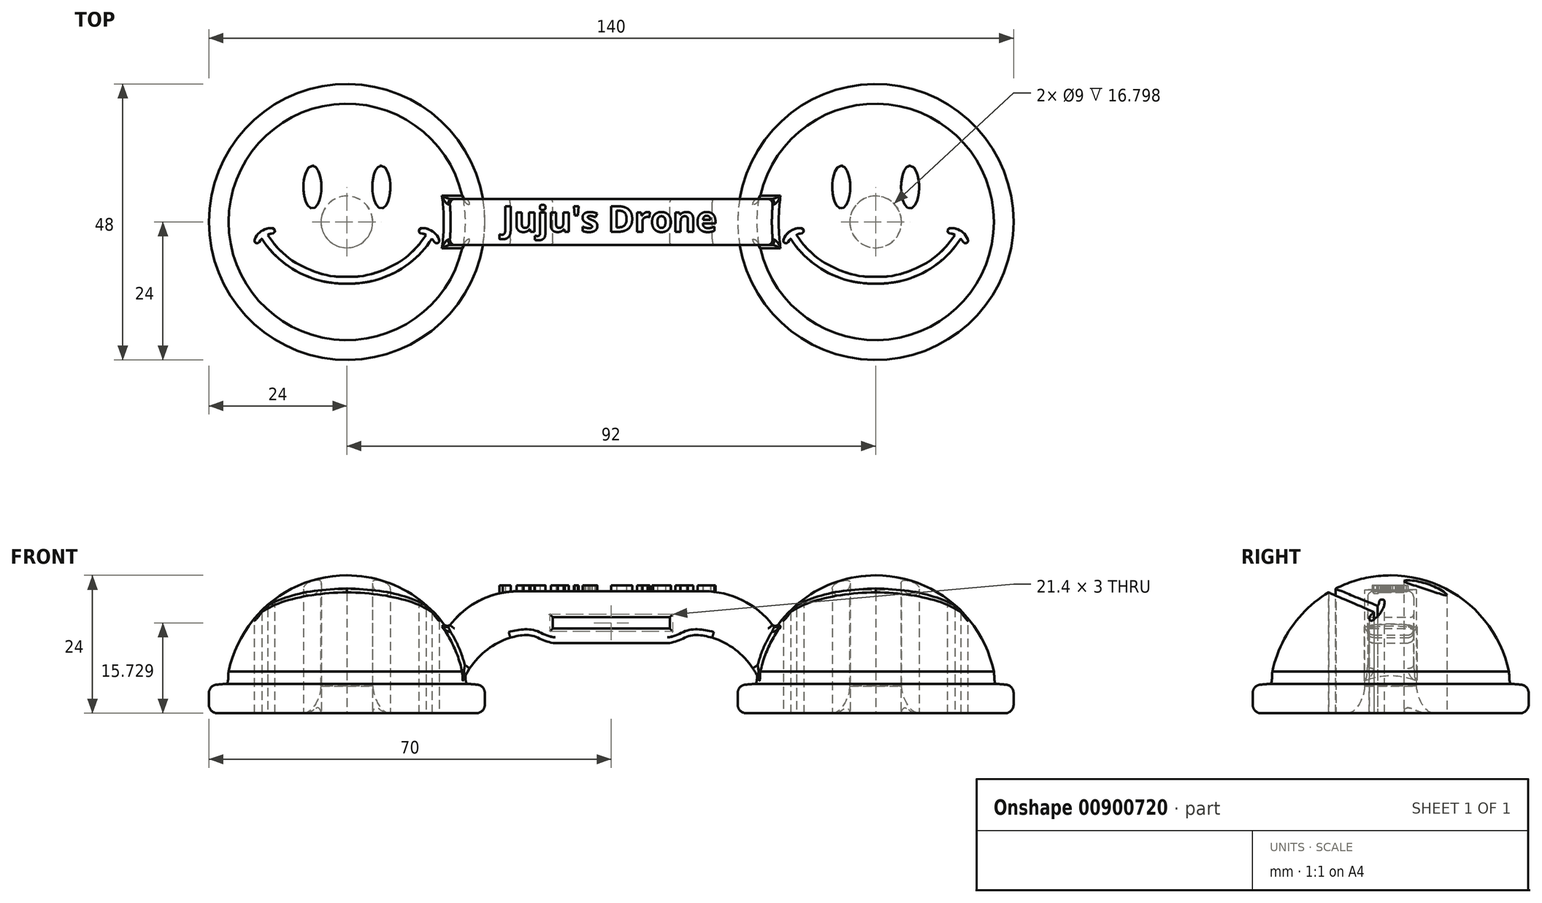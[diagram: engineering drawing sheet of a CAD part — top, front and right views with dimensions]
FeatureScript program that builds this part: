
annotation { "Feature Type Name" : "Feature", "Feature Type Description" : "" }
export const myFeature = defineFeature(function(context is Context, id is Id, definition is map)
    precondition{}
    {
        {
            var Q0;
            Q0=qCreatedBy(makeId("Front.planeOp"),FACE);
            var sketch = newSketch(context, id + "F0", { "sketchPlane" : qUnion([Q0])});
            skLineSegment(sketch, "E0", {"start": v(-24, 0) * mm, "end": v(-24, 5) * mm});
            skArc(sketch, "E1", {"start": v(0, 24) * mm, "mid": v(-13.27, 19.27) * mm, "end": v(-20.57, 7.23) * mm});
            skFitSpline(sketch, "E2", {"points": [v(-20.57, 7.23) * mm, v(-20.79, 5.27) * mm, v(-21.2, 5.12) * mm, v(-21.83, 5.04) * mm, v(-24, 5) * mm], "startDerivative": vector(-0.76, -2.02) * mm, "endDerivative": vector(-7.34, -0.04) * mm});
            skLineSegment(sketch, "E3", {"start": v(-24, 0) * mm, "end": v(-7.5, 0) * mm});
            skLineSegment(sketch, "E4", {"start": v(0, 24) * mm, "end": v(0, 21.5) * mm});
            skLineSegment(sketch, "E5", {"start": v(0, 21.5) * mm, "end": v(-4.5, 21.5) * mm});
            skLineSegment(sketch, "E6", {"start": v(-4.5, 21.5) * mm, "end": v(-4.5, 4.7) * mm});
            skFitSpline(sketch, "E7", {"points": [v(-4.5, 4.7) * mm, v(-4.72, 3.38) * mm, v(-5.02, 2.5) * mm, v(-5.7, 1.24) * mm, v(-6.66, 0.28) * mm, v(-7.5, 0) * mm], "startDerivative": vector(-0.9, -6.62) * mm, "endDerivative": vector(-4.88, -1.03) * mm});
            skSolve(sketch);
        }
        {
            var Q0;
            Q0 = qSketchRegion(id + "F0", true);
            var Q1;
            Q1=sQuery(id+"F0.wireOp",EDGE,"E4");
            revolve(context, id + "F1", {"surfaceOperationType" : NewSurfaceOperationType.NEW, "entities" : qUnion([Q0]), "axis" : qUnion([Q1]), "revolveType" : RevolveType.FULL});
        }
        {
            var Q0;
            Q0=qCreatedBy(makeId("Top.planeOp"),FACE);
            var sketch = newSketch(context, id + "F2", { "sketchPlane" : qUnion([Q0])});
            skEllipse(sketch, "E8", {"center": v(-6, 6.07) * mm, "majorRadius": 3.74 * mm, "minorRadius": 1.57 * mm, "majorAxis": v(0, 1)});
            skLineSegment(sketch, "E9", {"start": v(0, -9.53) * mm, "end": v(0, -10.75) * mm});
            skFitSpline(sketch, "E10", {"points": [v(0, -9.53) * mm, v(-1.6, -9.53) * mm, v(-4.06, -9.12) * mm, v(-6.52, -8.28) * mm, v(-8.7, -7.21) * mm, v(-10.27, -6.15) * mm, v(-12.28, -4.24) * mm, v(-13.22, -3.03) * mm, v(-13.79, -2.28) * mm], "startDerivative": vector(-13.49, -0.52) * mm, "endDerivative": vector(-6.38, 8.41) * mm});
            skFitSpline(sketch, "E11", {"points": [v(-13.79, -2.28) * mm, v(-13.34, -2.04) * mm, v(-13, -2) * mm, v(-12.74, -1.93) * mm, v(-12.54, -1.7) * mm, v(-12.5, -1.46) * mm, v(-12.63, -1.23) * mm, v(-12.76, -1.12) * mm, v(-13.08, -1.08) * mm, v(-13.63, -1.1) * mm, v(-14.18, -1.25) * mm, v(-14.79, -1.54) * mm, v(-15.41, -2.05) * mm, v(-15.7, -2.41) * mm, v(-15.92, -2.8) * mm, v(-16.04, -3.05) * mm, v(-16.08, -3.27) * mm, v(-16.04, -3.47) * mm, v(-15.93, -3.58) * mm, v(-15.8, -3.67) * mm, v(-15.6, -3.7) * mm, v(-15.43, -3.66) * mm, v(-15.28, -3.53) * mm, v(-15.1, -3.31) * mm, v(-14.98, -3.15) * mm, v(-14.8, -2.92) * mm], "startDerivative": vector(8.98, 5.76) * mm, "endDerivative": vector(5.3, 6.14) * mm});
            skFitSpline(sketch, "E12", {"points": [v(-14.8, -2.92) * mm, v(-14.11, -3.9) * mm, v(-12.74, -5.51) * mm, v(-11.31, -6.82) * mm, v(-9.19, -8.33) * mm, v(-7.25, -9.31) * mm, v(-4.65, -10.21) * mm, v(-1.98, -10.66) * mm, v(0, -10.75) * mm], "startDerivative": vector(6.45, -9.82) * mm, "endDerivative": vector(15.88, 0.35) * mm});
            skSolve(sketch);
        }
        {
            var Q0;
            Q0 = qSketchRegion(id + "F2", true);
            extrude(context, id + "F3", {"entities" : qUnion([Q0]), "depth" : 45 * mm, "offsetDistance" : 25 * mm});
        }
        {
            var Q0;
            Q0=makeQuery(id+"F3.opExtrude","SWEPT_BODY",BODY,{"disambiguationData":[OSD([sQuery(id+"F2.wireOp",EDGE,"E8")])]});
            var Q1;
            Q1=makeQuery(id+"F3.opExtrude","SWEPT_BODY",BODY,{"disambiguationData":[OSD([sQuery(id+"F2.wireOp",EDGE,"E9"),sQuery(id+"F2.wireOp",EDGE,"E10"),sQuery(id+"F2.wireOp",EDGE,"E11"),sQuery(id+"F2.wireOp",EDGE,"E12")])]});
            var Q2;
            Q2=qCreatedBy(makeId("Right.planeOp"),FACE);
            mirror(context, id + "F4", {"entities" : qUnion([Q0, Q1]), "mirrorPlane" : qUnion([Q2])});
        }
        {
            var Q0;
            Q0=makeQuery(id+"F3.opExtrude","SWEPT_BODY",BODY,{"disambiguationData":[OSD([sQuery(id+"F2.wireOp",EDGE,"E8")])]});
            var Q1;
            Q1=makeQuery(id+"F3.opExtrude","SWEPT_BODY",BODY,{"disambiguationData":[OSD([sQuery(id+"F2.wireOp",EDGE,"E9"),sQuery(id+"F2.wireOp",EDGE,"E10"),sQuery(id+"F2.wireOp",EDGE,"E11"),sQuery(id+"F2.wireOp",EDGE,"E12")])]});
            var Q2;
            Q2=makeQuery(id+"F4.opPattern","COPY",BODY,{"derivedFrom":makeQuery(id+"F3.opExtrude","SWEPT_BODY",BODY,{"disambiguationData":[OSD([sQuery(id+"F2.wireOp",EDGE,"E8")])]}),"instanceName":"1"});
            var Q3;
            Q3=makeQuery(id+"F4.opPattern","COPY",BODY,{"derivedFrom":makeQuery(id+"F3.opExtrude","SWEPT_BODY",BODY,{"disambiguationData":[OSD([sQuery(id+"F2.wireOp",EDGE,"E9"),sQuery(id+"F2.wireOp",EDGE,"E10"),sQuery(id+"F2.wireOp",EDGE,"E11"),sQuery(id+"F2.wireOp",EDGE,"E12")])]}),"instanceName":"1"});
            var Q4;
            Q4=makeQuery(id+"F1.opRevolve","SWEPT_BODY",BODY,{"disambiguationData":[OSD([sQuery(id+"F0.wireOp",EDGE,"E0"),sQuery(id+"F0.wireOp",EDGE,"E1"),sQuery(id+"F0.wireOp",EDGE,"E2"),sQuery(id+"F0.wireOp",EDGE,"E3"),sQuery(id+"F0.wireOp",EDGE,"E4"),sQuery(id+"F0.wireOp",EDGE,"E5"),sQuery(id+"F0.wireOp",EDGE,"E6"),sQuery(id+"F0.wireOp",EDGE,"E7")])]});
            booleanBodies(context, id + "F5", {"operationType" : BooleanOperationType.SUBTRACTION, "tools" : qUnion([Q0, Q1, Q2, Q3]), "targets" : qUnion([Q4])});
        }
        {
            var Q0;
            Q0=makeQuery(id+"F1.opRevolve","SWEPT_EDGE",EDGE,{"disambiguationData":[OSD([sQuery(id+"F0.wireOp",EDGE,"E0"),sQuery(id+"F0.wireOp",EDGE,"E3")])]});
            var Q1;
            Q1=makeQuery(id+"F1.opRevolve","SWEPT_EDGE",EDGE,{"disambiguationData":[OSD([sQuery(id+"F0.wireOp",EDGE,"E0"),sQuery(id+"F0.wireOp",EDGE,"E2")])]});
            var Q2;
            Q2=makeQuery(id+"F5.opBoolean","SPLIT",EDGE,{"disambiguationData":[OD(1.0)],"derivedFrom":makeQuery(id+"F1.opRevolve","SWEPT_EDGE",EDGE,{"disambiguationData":[OSD([sQuery(id+"F0.wireOp",EDGE,"E3"),sQuery(id+"F0.wireOp",EDGE,"E7")])]})});
            var Q3;
            Q3=makeQuery(id+"F5.opBoolean","SPLIT",EDGE,{"disambiguationData":[OD(0.0)],"derivedFrom":makeQuery(id+"F1.opRevolve","SWEPT_EDGE",EDGE,{"disambiguationData":[OSD([sQuery(id+"F0.wireOp",EDGE,"E3"),sQuery(id+"F0.wireOp",EDGE,"E7")])]})});
            fillet(context, id + "F6", {"entities" : qUnion([Q0, Q1, Q2, Q3]), "radius" : 1.5 * mm, "tangentPropagation" : true, "allowEdgeOverflow" : false});
        }
        {
            var Q0;
            Q0=qCreatedBy(makeId("Right.planeOp"),FACE);
            cPlane(context, id + "F7", {"entities" : qUnion([Q0]), "cplaneType" : CPlaneType.OFFSET, "offset" : 46 * mm, "width" : 150 * mm, "height" : 150 * mm});
        }
        {
            var Q0;
            Q0=qCreatedBy(makeId("Front.planeOp"),FACE);
            var sketch = newSketch(context, id + "F8", { "sketchPlane" : qUnion([Q0])});
            skLineSegment(sketch, "E13", {"start": v(46, 12.23) * mm, "end": v(46, 14.73) * mm});
            skLineSegment(sketch, "E14", {"start": v(46, 21.23) * mm, "end": v(29.83, 21.23) * mm});
            skArc(sketch, "E15", {"start": v(28.43, 13.17) * mm, "mid": v(23.57, 10.37) * mm, "end": v(20.27, 5.83) * mm});
            skArc(sketch, "E16", {"start": v(29.83, 21.23) * mm, "mid": v(22.54, 19.33) * mm, "end": v(17.1, 14.13) * mm});
            skLineSegment(sketch, "E17", {"start": v(17.1, 14.13) * mm, "end": v(20.27, 5.83) * mm});
            skLineSegment(sketch, "E18", {"start": v(46, 12.23) * mm, "end": v(36.24, 12.23) * mm});
            skFitSpline(sketch, "E19", {"points": [v(28.43, 13.17) * mm, v(31.25, 13.62) * mm, v(32.88, 13.32) * mm, v(33.92, 12.8) * mm, v(34.8, 12.52) * mm, v(35.53, 12.29) * mm, v(36.24, 12.23) * mm], "startDerivative": vector(15.62, 3.56) * mm, "endDerivative": vector(6.76, 0.01) * mm});
            skLineSegment(sketch, "E20", {"start": v(46, 14.73) * mm, "end": v(35.8, 14.73) * mm});
            skLineSegment(sketch, "E21", {"start": v(35.8, 14.73) * mm, "end": v(35.8, 16.73) * mm});
            skLineSegment(sketch, "E22", {"start": v(35.8, 16.73) * mm, "end": v(46, 16.73) * mm});
            skLineSegment(sketch, "E23.trimOffspring", {"start": v(46, 16.73) * mm, "end": v(46, 21.23) * mm});
            skSolve(sketch);
        }
        {
            var Q0;
            Q0 = qSketchRegion(id + "F8", true);
            extrude(context, id + "F9", {"entities" : qUnion([Q0]), "operationType" : NewBodyOperationType.ADD, "endBound" : BoundingType.SYMMETRIC, "depth" : 8 * mm, "offsetDistance" : 25 * mm});
        }
        {
            var Q0;
            Q0=makeQuery(id+"F9.boolean.opBoolean","INTERSECT",EDGE,{"derivedFrom":[makeQuery(id+"F1.opRevolve","SWEPT_FACE",FACE,{"disambiguationData":[OSD([sQuery(id+"F0.wireOp",EDGE,"E1")])]}),makeQuery(id+"F9.opExtrude","SWEPT_FACE",FACE,{"disambiguationData":[OSD([sQuery(id+"F8.wireOp",EDGE,"E16")])]})]});
            var Q1;
            Q1=makeQuery(id+"F9.boolean.opBoolean","INTERSECT",EDGE,{"derivedFrom":[makeQuery(id+"F1.opRevolve","SWEPT_FACE",FACE,{"disambiguationData":[OSD([sQuery(id+"F0.wireOp",EDGE,"E1")])]}),makeQuery(id+"F9.opExtrude","CAP_FACE",FACE,{"disambiguationData":[OSD([sQuery(id+"F8.wireOp",EDGE,"E13"),sQuery(id+"F8.wireOp",EDGE,"E14"),sQuery(id+"F8.wireOp",EDGE,"E15"),sQuery(id+"F8.wireOp",EDGE,"E16"),sQuery(id+"F8.wireOp",EDGE,"E17"),sQuery(id+"F8.wireOp",EDGE,"E18"),sQuery(id+"F8.wireOp",EDGE,"E19"),sQuery(id+"F8.wireOp",EDGE,"E20"),sQuery(id+"F8.wireOp",EDGE,"E21"),sQuery(id+"F8.wireOp",EDGE,"E22"),sQuery(id+"F8.wireOp",EDGE,"E23.trimOffspring")])],"isStart":false})]});
            var Q2;
            Q2=makeQuery(id+"F9.boolean.opBoolean","INTERSECT",EDGE,{"derivedFrom":[makeQuery(id+"F1.opRevolve","SWEPT_FACE",FACE,{"disambiguationData":[OSD([sQuery(id+"F0.wireOp",EDGE,"E2")])]}),makeQuery(id+"F9.opExtrude","CAP_FACE",FACE,{"disambiguationData":[OSD([sQuery(id+"F8.wireOp",EDGE,"E13"),sQuery(id+"F8.wireOp",EDGE,"E14"),sQuery(id+"F8.wireOp",EDGE,"E15"),sQuery(id+"F8.wireOp",EDGE,"E16"),sQuery(id+"F8.wireOp",EDGE,"E17"),sQuery(id+"F8.wireOp",EDGE,"E18"),sQuery(id+"F8.wireOp",EDGE,"E19"),sQuery(id+"F8.wireOp",EDGE,"E20"),sQuery(id+"F8.wireOp",EDGE,"E21"),sQuery(id+"F8.wireOp",EDGE,"E22"),sQuery(id+"F8.wireOp",EDGE,"E23.trimOffspring")])],"isStart":false})]});
            var Q3;
            Q3=makeQuery(id+"F9.boolean.opBoolean","INTERSECT",EDGE,{"derivedFrom":[makeQuery(id+"F1.opRevolve","SWEPT_FACE",FACE,{"disambiguationData":[OSD([sQuery(id+"F0.wireOp",EDGE,"E1")])]}),makeQuery(id+"F9.opExtrude","CAP_FACE",FACE,{"disambiguationData":[OSD([sQuery(id+"F8.wireOp",EDGE,"E13"),sQuery(id+"F8.wireOp",EDGE,"E14"),sQuery(id+"F8.wireOp",EDGE,"E15"),sQuery(id+"F8.wireOp",EDGE,"E16"),sQuery(id+"F8.wireOp",EDGE,"E17"),sQuery(id+"F8.wireOp",EDGE,"E18"),sQuery(id+"F8.wireOp",EDGE,"E19"),sQuery(id+"F8.wireOp",EDGE,"E20"),sQuery(id+"F8.wireOp",EDGE,"E21"),sQuery(id+"F8.wireOp",EDGE,"E22"),sQuery(id+"F8.wireOp",EDGE,"E23.trimOffspring")])],"isStart":true})]});
            var Q4;
            Q4=makeQuery(id+"F9.boolean.opBoolean","INTERSECT",EDGE,{"derivedFrom":[makeQuery(id+"F1.opRevolve","SWEPT_FACE",FACE,{"disambiguationData":[OSD([sQuery(id+"F0.wireOp",EDGE,"E2")])]}),makeQuery(id+"F9.opExtrude","CAP_FACE",FACE,{"disambiguationData":[OSD([sQuery(id+"F8.wireOp",EDGE,"E13"),sQuery(id+"F8.wireOp",EDGE,"E14"),sQuery(id+"F8.wireOp",EDGE,"E15"),sQuery(id+"F8.wireOp",EDGE,"E16"),sQuery(id+"F8.wireOp",EDGE,"E17"),sQuery(id+"F8.wireOp",EDGE,"E18"),sQuery(id+"F8.wireOp",EDGE,"E19"),sQuery(id+"F8.wireOp",EDGE,"E20"),sQuery(id+"F8.wireOp",EDGE,"E21"),sQuery(id+"F8.wireOp",EDGE,"E22"),sQuery(id+"F8.wireOp",EDGE,"E23.trimOffspring")])],"isStart":true})]});
            fillet(context, id + "F10", {"entities" : qUnion([Q0, Q1, Q2, Q3, Q4]), "radius" : 0.75 * mm, "tangentPropagation" : true, "allowEdgeOverflow" : false});
        }
        {
            var Q0;
            Q0=makeQuery(id+"F9.opExtrude","CAP_EDGE",EDGE,{"disambiguationData":[OSD([sQuery(id+"F8.wireOp",EDGE,"E15")])],"isStart":false});
            var Q1;
            Q1=makeQuery(id+"F9.opExtrude","CAP_EDGE",EDGE,{"disambiguationData":[OSD([sQuery(id+"F8.wireOp",EDGE,"E19")])],"isStart":false});
            var Q2;
            Q2=makeQuery(id+"F9.opExtrude","CAP_EDGE",EDGE,{"disambiguationData":[OSD([sQuery(id+"F8.wireOp",EDGE,"E18")])],"isStart":false});
            var Q3;
            Q3=makeQuery(id+"F9.opExtrude","CAP_EDGE",EDGE,{"disambiguationData":[OSD([sQuery(id+"F8.wireOp",EDGE,"E16")])],"isStart":false});
            var Q4;
            Q4=makeQuery(id+"F9.opExtrude","CAP_EDGE",EDGE,{"disambiguationData":[OSD([sQuery(id+"F8.wireOp",EDGE,"E14")])],"isStart":false});
            var Q5;
            Q5=makeQuery(id+"F9.opExtrude","CAP_EDGE",EDGE,{"disambiguationData":[OSD([sQuery(id+"F8.wireOp",EDGE,"E16")])],"isStart":true});
            var Q6;
            Q6=makeQuery(id+"F9.opExtrude","CAP_EDGE",EDGE,{"disambiguationData":[OSD([sQuery(id+"F8.wireOp",EDGE,"E14")])],"isStart":true});
            var Q7;
            Q7=makeQuery(id+"F9.opExtrude","CAP_EDGE",EDGE,{"disambiguationData":[OSD([sQuery(id+"F8.wireOp",EDGE,"E18")])],"isStart":true});
            var Q8;
            Q8=makeQuery(id+"F9.opExtrude","CAP_EDGE",EDGE,{"disambiguationData":[OSD([sQuery(id+"F8.wireOp",EDGE,"E19")])],"isStart":true});
            var Q9;
            Q9=makeQuery(id+"F9.opExtrude","CAP_EDGE",EDGE,{"disambiguationData":[OSD([sQuery(id+"F8.wireOp",EDGE,"E15")])],"isStart":true});
            fillet(context, id + "F11", {"entities" : qUnion([Q0, Q1, Q2, Q3, Q4, Q5, Q6, Q7, Q8, Q9]), "radius" : 1 * mm, "tangentPropagation" : true, "allowEdgeOverflow" : false});
        }
        {
            var Q0;
            Q0=makeQuery(id+"F1.opRevolve","SWEPT_BODY",BODY,{"disambiguationData":[OSD([sQuery(id+"F0.wireOp",EDGE,"E0"),sQuery(id+"F0.wireOp",EDGE,"E1"),sQuery(id+"F0.wireOp",EDGE,"E2"),sQuery(id+"F0.wireOp",EDGE,"E3"),sQuery(id+"F0.wireOp",EDGE,"E4"),sQuery(id+"F0.wireOp",EDGE,"E5"),sQuery(id+"F0.wireOp",EDGE,"E6"),sQuery(id+"F0.wireOp",EDGE,"E7")])]});
            var Q1;
            Q1=qCreatedBy(id+"F7.planeOp",FACE);
            mirror(context, id + "F12", {"operationType" : NewBodyOperationType.ADD, "entities" : qUnion([Q0]), "mirrorPlane" : qUnion([Q1])});
        }
        {
            var Q0;
            {var subQ0=makeQuery(id+"F9.opExtrude","CAP_EDGE",EDGE,{"disambiguationData":[OSD([sQuery(id+"F8.wireOp",EDGE,"E22")])],"isStart":false});Q0=makeQuery(id+"F12.boolean.opBoolean","MERGE",EDGE,{"derivedFrom":[subQ0,makeQuery(id+"F12.opPattern","COPY",EDGE,{"derivedFrom":subQ0,"instanceName":"1"})]});}
            var Q1;
            Q1=makeQuery(id+"F9.opExtrude","CAP_EDGE",EDGE,{"disambiguationData":[OSD([sQuery(id+"F8.wireOp",EDGE,"E21")])],"isStart":false});
            var Q2;
            {var subQ0=makeQuery(id+"F9.opExtrude","CAP_EDGE",EDGE,{"disambiguationData":[OSD([sQuery(id+"F8.wireOp",EDGE,"E20")])],"isStart":false});Q2=makeQuery(id+"F12.boolean.opBoolean","MERGE",EDGE,{"derivedFrom":[subQ0,makeQuery(id+"F12.opPattern","COPY",EDGE,{"derivedFrom":subQ0,"instanceName":"1"})]});}
            var Q3;
            Q3=makeQuery(id+"F12.opPattern","COPY",EDGE,{"derivedFrom":makeQuery(id+"F9.opExtrude","CAP_EDGE",EDGE,{"disambiguationData":[OSD([sQuery(id+"F8.wireOp",EDGE,"E21")])],"isStart":false}),"instanceName":"1"});
            var Q4;
            Q4=makeQuery(id+"F9.opExtrude","CAP_EDGE",EDGE,{"disambiguationData":[OSD([sQuery(id+"F8.wireOp",EDGE,"E21")])],"isStart":true});
            var Q5;
            {var subQ0=makeQuery(id+"F9.opExtrude","CAP_EDGE",EDGE,{"disambiguationData":[OSD([sQuery(id+"F8.wireOp",EDGE,"E20")])],"isStart":true});Q5=makeQuery(id+"F12.boolean.opBoolean","MERGE",EDGE,{"derivedFrom":[subQ0,makeQuery(id+"F12.opPattern","COPY",EDGE,{"derivedFrom":subQ0,"instanceName":"1"})]});}
            var Q6;
            {var subQ0=makeQuery(id+"F9.opExtrude","CAP_EDGE",EDGE,{"disambiguationData":[OSD([sQuery(id+"F8.wireOp",EDGE,"E22")])],"isStart":true});Q6=makeQuery(id+"F12.boolean.opBoolean","MERGE",EDGE,{"derivedFrom":[subQ0,makeQuery(id+"F12.opPattern","COPY",EDGE,{"derivedFrom":subQ0,"instanceName":"1"})]});}
            var Q7;
            Q7=makeQuery(id+"F12.opPattern","COPY",EDGE,{"derivedFrom":makeQuery(id+"F9.opExtrude","CAP_EDGE",EDGE,{"disambiguationData":[OSD([sQuery(id+"F8.wireOp",EDGE,"E21")])],"isStart":true}),"instanceName":"1"});
            fillet(context, id + "F13", {"entities" : qUnion([Q0, Q1, Q2, Q3, Q4, Q5, Q6, Q7]), "radius" : 0.5 * mm, "tangentPropagation" : true, "allowEdgeOverflow" : false});
        }
        {
            var Q0;
            {var subQ0=makeQuery(id+"F9.opExtrude","SWEPT_FACE",FACE,{"disambiguationData":[OSD([sQuery(id+"F8.wireOp",EDGE,"E14")])]});Q0=makeQuery(id+"F12.boolean.opBoolean","MERGE",FACE,{"derivedFrom":[subQ0,makeQuery(id+"F12.opPattern","COPY",FACE,{"derivedFrom":subQ0,"instanceName":"1"})]});}
            var sketch = newSketch(context, id + "F14", { "sketchPlane" : qUnion([Q0])});
            skText(sketch, "E24", { "text": "Juju\'s Drone", "fontName": "OpenSans-Bold.ttf"});
            const initialGuessF14  = {"E24": [0.027, -0.00171, 1, 0, 0.00446]};
            skSetInitialGuess(sketch, initialGuessF14);
            skSolve(sketch);
        }
        {
            var Q0;
            Q0 = qSketchRegion(id + "F14", true);
            extrude(context, id + "F15", {"entities" : qUnion([Q0]), "operationType" : NewBodyOperationType.ADD, "endBound" : BoundingType.SYMMETRIC, "depth" : 2 * mm, "offsetDistance" : 25 * mm});
        }
    });
